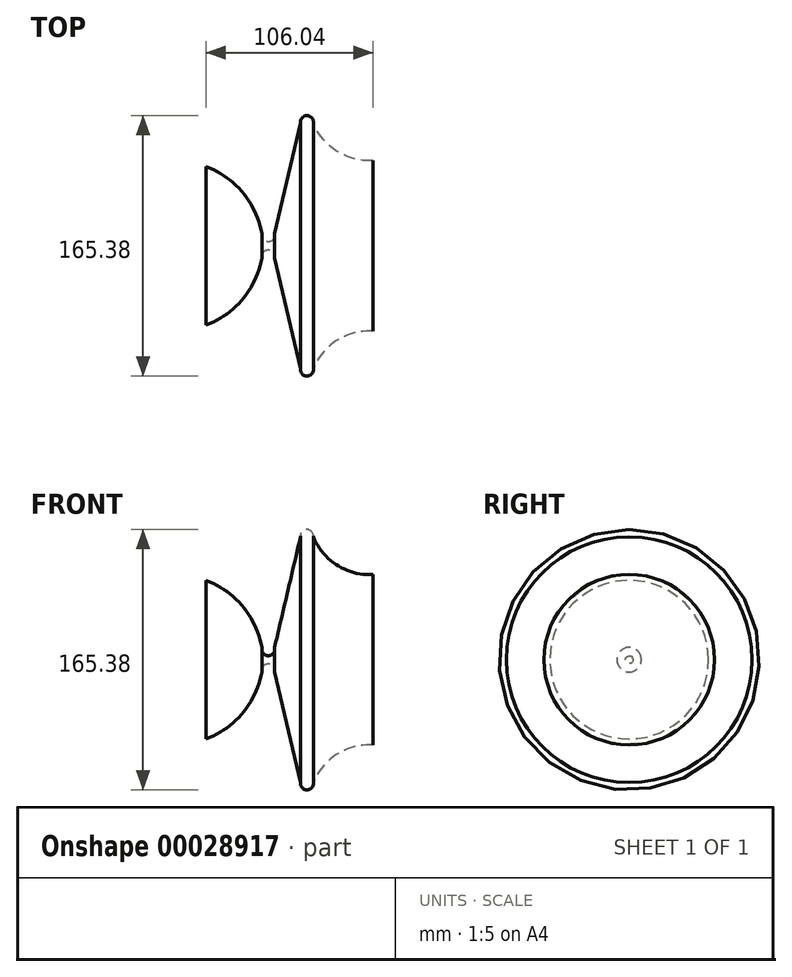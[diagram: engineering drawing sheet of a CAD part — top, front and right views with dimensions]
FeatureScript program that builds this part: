
annotation { "Feature Type Name" : "Feature", "Feature Type Description" : "" }
export const myFeature = defineFeature(function(context is Context, id is Id, definition is map)
    precondition{}
    {
        {
            var Q0;
            Q0=qCreatedBy(makeId("Front.planeOp"),FACE);
            var sketch = newSketch(context, id + "F0", { "sketchPlane" : qUnion([Q0])});
            skArc(sketch, "E0", {"start": v(-8.03, -25.28) * mm, "mid": v(-20.18, 0.68) * mm, "end": v(-43.52, 17.3) * mm});
            skArc(sketch, "E1", {"start": v(-8.03, -25.28) * mm, "mid": v(-4.02, -30.56) * mm, "end": v(0, -25.28) * mm});
            skLineSegment(sketch, "E2", {"start": v(0, -25.28) * mm, "end": v(16.45, 45) * mm});
            skArc(sketch, "E3", {"start": v(24.62, 45) * mm, "mid": v(20.53, 49.63) * mm, "end": v(16.45, 45) * mm});
            skArc(sketch, "E4", {"start": v(24.62, 45) * mm, "mid": v(39.7, 26.92) * mm, "end": v(62.52, 21.1) * mm});
            skLineSegment(sketch, "E5", {"start": v(-43.52, 17.3) * mm, "end": v(-43.52, -33.06) * mm});
            skLineSegment(sketch, "E6", {"start": v(-43.52, -33.06) * mm, "end": v(62.52, -33.06) * mm});
            skLineSegment(sketch, "E7", {"start": v(62.52, 21.1) * mm, "end": v(62.52, -33.06) * mm});
            skSolve(sketch);
        }
        {
            var Q0;
            Q0=makeQuery(id+"F0.imprint","IMPRINT",FACE,{"disambiguationData":[TD([[makeQuery(id+"F0.imprint","IMPRINT",EDGE,{"derivedFrom":sQuery(id+"F0.wireOp",EDGE,"E0")}),1.0]])]});
            var Q1;
            Q1=sQuery(id+"F0.wireOp",EDGE,"E6");
            revolve(context, id + "F1", {"entities" : qUnion([Q0]), "axis" : qUnion([Q1]), "revolveType" : RevolveType.FULL});
        }
    });
